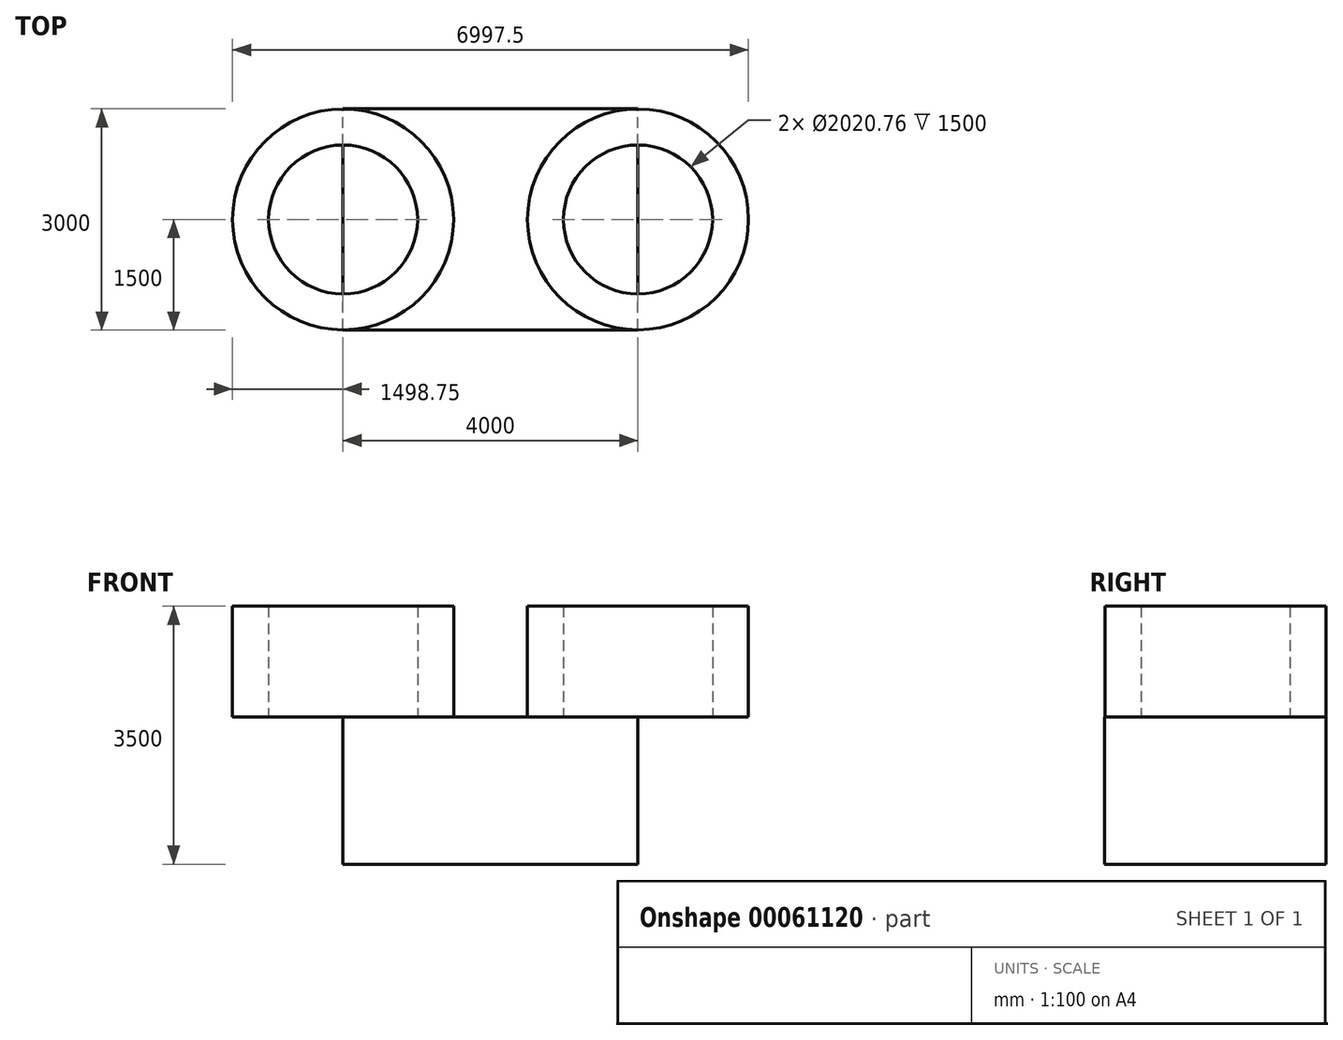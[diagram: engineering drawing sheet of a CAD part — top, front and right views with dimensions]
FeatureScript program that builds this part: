
annotation { "Feature Type Name" : "Feature", "Feature Type Description" : "" }
export const myFeature = defineFeature(function(context is Context, id is Id, definition is map)
    precondition{}
    {
        {
            var Q0;
            Q0=qCreatedBy(makeId("Top.planeOp"),FACE);
            var sketch = newSketch(context, id + "F0", { "sketchPlane" : qUnion([Q0])});
            skLineSegment(sketch, "E0.rect.bottom", {"start": v(2000, -1500) * mm, "end": v(-2000, -1500) * mm});
            skLineSegment(sketch, "E0.rect.top", {"start": v(2000, 1500) * mm, "end": v(-2000, 1500) * mm});
            skLineSegment(sketch, "E0.rect.left", {"start": v(2000, -1500) * mm, "end": v(2000, 1500) * mm});
            skLineSegment(sketch, "E0.rect.right", {"start": v(-2000, -1500) * mm, "end": v(-2000, 1500) * mm});
            skPoint(sketch, "E0.rect.middle", {"position": v(0, 0) * mm});
            skSolve(sketch);
        }
        {
            var Q0;
            Q0 = qSketchRegion(id + "F0", true);
            extrude(context, id + "F1", {"entities" : qUnion([Q0]), "depth" : 2000 * mm});
        }
        {
            var Q0;
            Q0=makeQuery(id+"F1.opExtrude","CAP_FACE",FACE,{"disambiguationData":[OSD([sQuery(id+"F0.wireOp",EDGE,"E0.rect.bottom"),sQuery(id+"F0.wireOp",EDGE,"E0.rect.top"),sQuery(id+"F0.wireOp",EDGE,"E0.rect.left"),sQuery(id+"F0.wireOp",EDGE,"E0.rect.right")])],"isStart":false});
            var sketch = newSketch(context, id + "F2", { "sketchPlane" : qUnion([Q0])});
            skCircle(sketch, "E1", {"center": v(-2000, 0) * mm, "radius": 1498.75 * mm});
            skCircle(sketch, "E2", {"center": v(-2000, 0) * mm, "radius": 1010.38 * mm});
            skLineSegment(sketch, "E3", {"start": v(0, 1500) * mm, "end": v(0, -1500) * mm});
            skCircle(sketch, "E4.MirrorC", {"center": v(2000, 0) * mm, "radius": 1010.38 * mm});
            skCircle(sketch, "E5.MirrorC", {"center": v(2000, 0) * mm, "radius": 1498.75 * mm});
            skSolve(sketch);
        }
        {
            var Q0;
            Q0 = qSketchRegion(id + "F2", true);
            extrude(context, id + "F3", {"entities" : qUnion([Q0]), "operationType" : NewBodyOperationType.ADD, "depth" : 1500 * mm});
        }
    });
